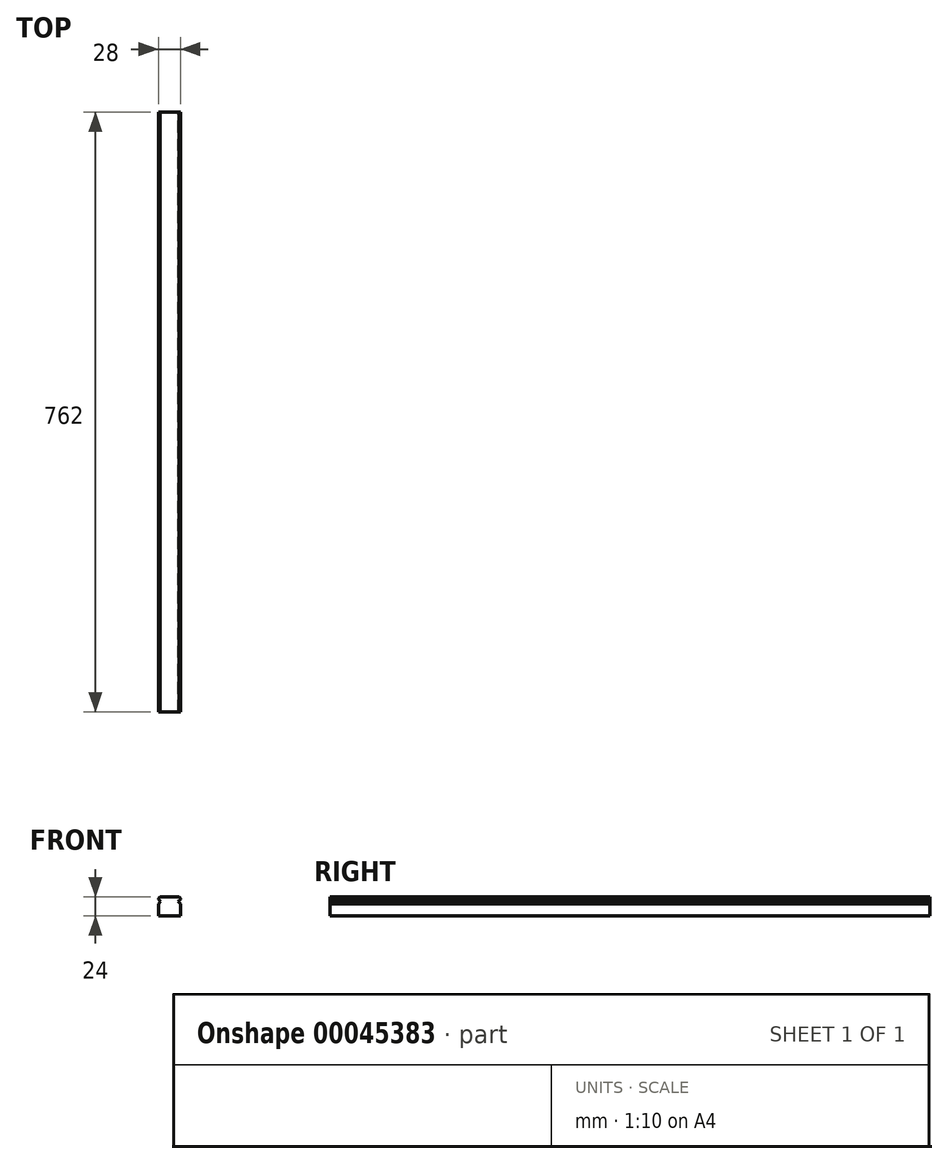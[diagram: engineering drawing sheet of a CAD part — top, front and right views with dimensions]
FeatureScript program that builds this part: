
annotation { "Feature Type Name" : "Feature", "Feature Type Description" : "" }
export const myFeature = defineFeature(function(context is Context, id is Id, definition is map)
    precondition{}
    {
        {
            var Q0;
            Q0=qCreatedBy(makeId("Front.planeOp"),FACE);
            var sketch = newSketch(context, id + "F0", { "sketchPlane" : qUnion([Q0])});
            skLineSegment(sketch, "E0.bottom", {"start": v(-9.9, 12.6) * mm, "end": v(13.87, 12.6) * mm});
            skLineSegment(sketch, "E0.top", {"start": v(-12.01, -11.4) * mm, "end": v(15.99, -11.4) * mm});
            skLineSegment(sketch, "E0.left", {"start": v(-12.01, 10.49) * mm, "end": v(-12.01, 9.49) * mm});
            skLineSegment(sketch, "E0.right", {"start": v(15.99, 10.49) * mm, "end": v(15.99, 9.49) * mm});
            skLineSegment(sketch, "E1", {"start": v(-9.9, 12.6) * mm, "end": v(-12.01, 10.49) * mm});
            skLineSegment(sketch, "E2", {"start": v(13.87, 12.6) * mm, "end": v(15.99, 10.49) * mm});
            skLineSegment(sketch, "E3", {"start": v(-12.01, 9.49) * mm, "end": v(-9.18, 6.66) * mm});
            skLineSegment(sketch, "E4", {"start": v(-9.18, 6.66) * mm, "end": v(-12.01, 3.83) * mm});
            skLineSegment(sketch, "E5", {"start": v(15.99, 9.49) * mm, "end": v(13.16, 6.66) * mm});
            skLineSegment(sketch, "E6", {"start": v(13.16, 6.66) * mm, "end": v(15.99, 3.83) * mm});
            skLineSegment(sketch, "E7.trimOffspring", {"start": v(-12.01, 3.83) * mm, "end": v(-12.01, -11.4) * mm});
            skLineSegment(sketch, "E8.trimOffspring", {"start": v(15.99, 3.83) * mm, "end": v(15.99, -11.4) * mm});
            skSolve(sketch);
        }
        {
            var Q0;
            Q0=qSketchRegion(id+"F0",true);
            extrude(context, id + "F1", {"entities" : qUnion([Q0]), "depth" : 762 * mm});
        }
    });
